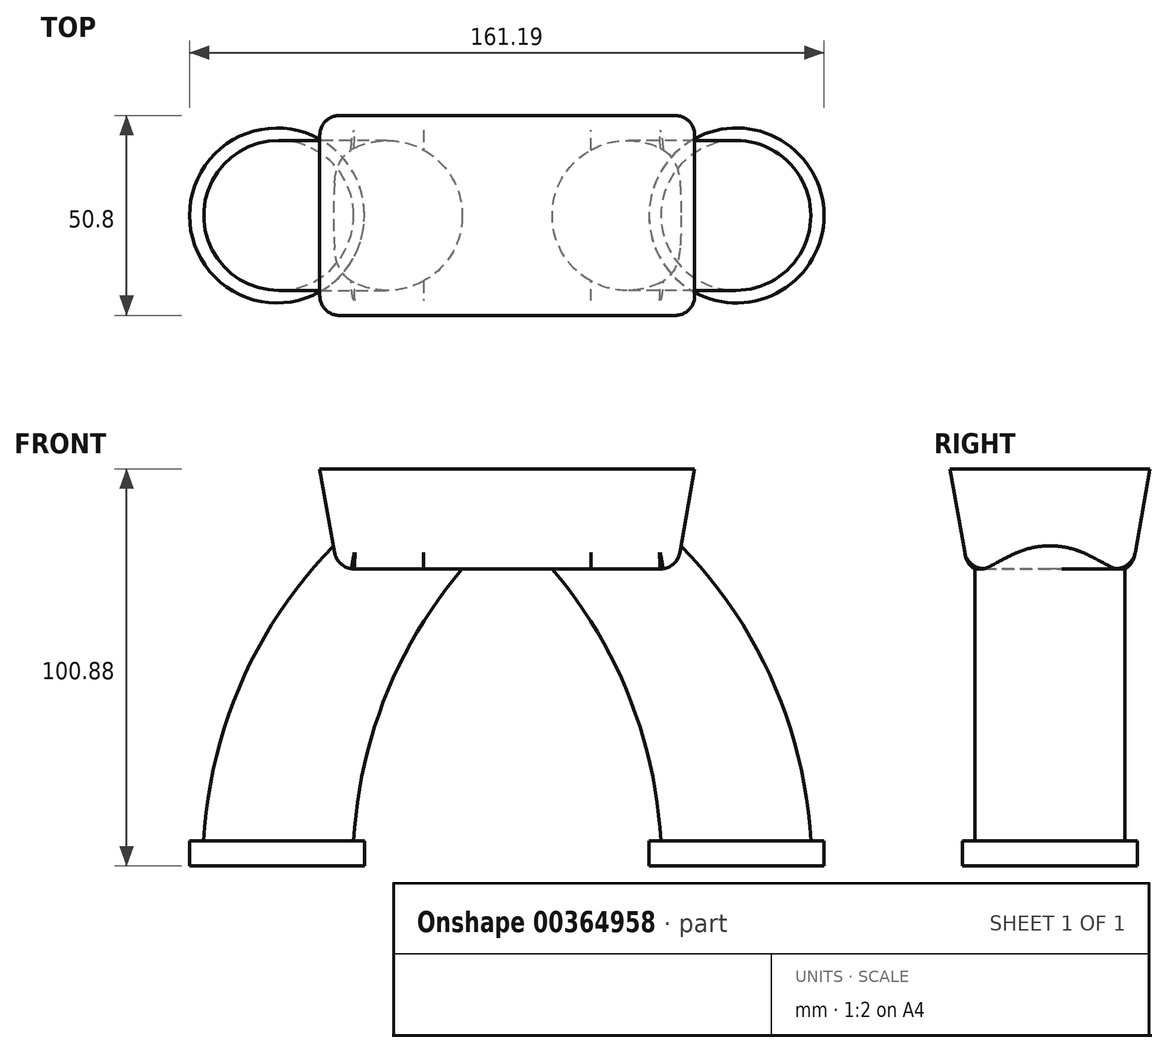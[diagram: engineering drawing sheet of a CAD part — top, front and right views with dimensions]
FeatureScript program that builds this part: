
annotation { "Feature Type Name" : "Feature", "Feature Type Description" : "" }
export const myFeature = defineFeature(function(context is Context, id is Id, definition is map)
    precondition{}
    {
        {
            var Q0;
            Q0=qCreatedBy(makeId("Top.planeOp"),FACE);
            var sketch = newSketch(context, id + "F0", { "sketchPlane" : qUnion([Q0])});
            skLineSegment(sketch, "E0", {"start": v(0, 0) * mm, "end": v(-116.48, 0) * mm, "construction": true});
            skCircle(sketch, "E1", {"center": v(-116.48, 0) * mm, "radius": 19.05 * mm});
            skCircle(sketch, "E2", {"center": v(0, 0) * mm, "radius": 19.05 * mm});
            skLineSegment(sketch, "E3.right", {"start": v(-140, -27.25) * mm, "end": v(-140, 27.25) * mm});
            skPoint(sketch, "E3.middle", {"position": v(-58.24, 0) * mm});
            skPoint(sketch, "E3.left.end.orphan", {"position": v(23.51, 27.25) * mm});
            skPoint(sketch, "E3.left.start.orphan", {"position": v(23.51, -27.25) * mm});
            skSolve(sketch);
        }
        {
            var Q0;
            Q0=qCreatedBy(makeId("Front.planeOp"),FACE);
            var sketch = newSketch(context, id + "F1", { "sketchPlane" : qUnion([Q0])});
            skArc(sketch, "E4", {"start": v(-58.24, 100.88) * mm, "mid": v(-100.88, 58.24) * mm, "end": v(-116.48, 0) * mm});
            skArc(sketch, "E5", {"start": v(0, 0) * mm, "mid": v(-15.6, 58.24) * mm, "end": v(-58.24, 100.88) * mm});
            skSolve(sketch);
        }
        {
            var Q0;
            Q0=makeQuery(id+"F0.imprint","IMPRINT",FACE,{"disambiguationData":[TD([[makeQuery(id+"F0.imprint","IMPRINT",EDGE,{"derivedFrom":sQuery(id+"F0.wireOp",EDGE,"E1")}),1.0]])]});
            var Q1;
            Q1=sQuery(id+"F1.wireOp",EDGE,"E4");
            sweep(context, id + "F2", {"profiles" : qUnion([Q0]), "path" : qUnion([Q1]), "keepProfileOrientation" : true});
        }
        {
            var Q0;
            Q0=makeQuery(id+"F0.imprint","IMPRINT",FACE,{"disambiguationData":[TD([[makeQuery(id+"F0.imprint","IMPRINT",EDGE,{"derivedFrom":sQuery(id+"F0.wireOp",EDGE,"E2")}),1.0]])]});
            var Q1;
            Q1=sQuery(id+"F1.wireOp",EDGE,"E5");
            sweep(context, id + "F3", {"operationType" : NewBodyOperationType.ADD, "profiles" : qUnion([Q0]), "path" : qUnion([Q1]), "keepProfileOrientation" : true});
        }
        {
            var Q0;
            Q0=qCreatedBy(makeId("Top.planeOp"),FACE);
            var sketch = newSketch(context, id + "F4", { "sketchPlane" : qUnion([Q0])});
            skCircle(sketch, "E6", {"center": v(-116.73, 0) * mm, "radius": 22.23 * mm});
            skCircle(sketch, "E7", {"center": v(0, 0) * mm, "radius": 22.23 * mm});
            skSolve(sketch);
        }
        {
            var Q0;
            Q0=makeQuery(id+"F4.imprint","IMPRINT",FACE,{"disambiguationData":[TD([[makeQuery(id+"F4.imprint","IMPRINT",EDGE,{"derivedFrom":sQuery(id+"F4.wireOp",EDGE,"E6")}),1.0]])]});
            var Q1;
            Q1=makeQuery(id+"F4.imprint","IMPRINT",FACE,{"disambiguationData":[TD([[makeQuery(id+"F4.imprint","IMPRINT",EDGE,{"derivedFrom":sQuery(id+"F4.wireOp",EDGE,"E7")}),1.0]])]});
            extrude(context, id + "F5", {"entities" : qUnion([Q0, Q1]), "operationType" : NewBodyOperationType.ADD, "depth" : 6.35 * mm});
        }
        {
            var Q0;
            Q0=makeQuery(id+"F2.opSweep","CAP_FACE",FACE,{"disambiguationData":[OSD([sQuery(id+"F0.wireOp",EDGE,"E1"),sQuery(id+"F1.wireOp",VERTEX,"E4.start")])],"isStart":false});
            var sketch = newSketch(context, id + "F6", { "sketchPlane" : qUnion([Q0])});
            skLineSegment(sketch, "E8.bottom", {"start": v(-32.84, -22.23) * mm, "end": v(-83.64, -22.22) * mm});
            skLineSegment(sketch, "E8.top", {"start": v(-32.84, 22.22) * mm, "end": v(-83.64, 22.23) * mm});
            skLineSegment(sketch, "E8.left", {"start": v(-32.84, -22.23) * mm, "end": v(-32.84, 22.23) * mm});
            skLineSegment(sketch, "E8.right", {"start": v(-83.64, -22.22) * mm, "end": v(-83.64, 22.23) * mm});
            skPoint(sketch, "E8.middle", {"position": v(-58.24, 0) * mm});
            skSolve(sketch);
        }
        {
            var Q0;
            Q0=makeQuery(id+"F6.imprint","IMPRINT",FACE,{"disambiguationData":[TD([[makeQuery(id+"F6.imprint","IMPRINT",EDGE,{"derivedFrom":sQuery(id+"F6.wireOp",EDGE,"E8.bottom")}),-1.0]])]});
            extrude(context, id + "F7", {"entities" : qUnion([Q0]), "operationType" : NewBodyOperationType.ADD, "oppositeDirection" : true, "depth" : 14.48 * mm, "hasSecondDirection" : true, "secondDirectionOppositeDirection" : true, "secondDirectionDepth" : 0.5 * mm, "hasSecondDirectionDraft" : true, "secondDirectionDraftAngle" : 4 * degree, "secondDirectionDraftPullDirection" : true});
        }
        {
            var Q0;
            Q0=makeQuery(id+"F7.opExtrude","CAP_EDGE",EDGE,{"disambiguationData":[OSD([sQuery(id+"F6.wireOp",EDGE,"E8.bottom")])],"isStart":false});
            var Q1;
            Q1=makeQuery(id+"F7.opExtrude","CAP_EDGE",EDGE,{"disambiguationData":[OSD([sQuery(id+"F6.wireOp",EDGE,"E8.top")])],"isStart":false});
            fillet(context, id + "F8", {"entities" : qUnion([Q0, Q1]), "radius" : 5.08 * mm, "tangentPropagation" : true, "allowEdgeOverflow" : false});
        }
        {
            var Q0;
            Q0=makeQuery(id+"F2.opSweep","CAP_FACE",FACE,{"disambiguationData":[OSD([sQuery(id+"F0.wireOp",EDGE,"E1"),sQuery(id+"F1.wireOp",VERTEX,"E4.start")])],"isStart":false});
            var sketch = newSketch(context, id + "F9", { "sketchPlane" : qUnion([Q0])});
            skLineSegment(sketch, "E9.bottom", {"start": v(-10.62, 25.4) * mm, "end": v(-105.87, 25.4) * mm});
            skLineSegment(sketch, "E9.top", {"start": v(-10.62, -25.4) * mm, "end": v(-105.87, -25.4) * mm});
            skLineSegment(sketch, "E9.left", {"start": v(-10.62, 25.4) * mm, "end": v(-10.62, -25.4) * mm});
            skLineSegment(sketch, "E9.right", {"start": v(-105.87, 25.4) * mm, "end": v(-105.87, -25.4) * mm});
            skPoint(sketch, "E9.middle", {"position": v(-58.24, 0) * mm});
            skSolve(sketch);
        }
        {
            var Q0;
            Q0=makeQuery(id+"F9.imprint","IMPRINT",FACE,{"disambiguationData":[TD([[makeQuery(id+"F9.imprint","IMPRINT",EDGE,{"derivedFrom":sQuery(id+"F9.wireOp",EDGE,"E9.bottom")}),1.0]])]});
            var Q1;
            {var subQ0=makeQuery(id+"F2.opSweep","CAP_EDGE",EDGE,{"disambiguationData":[OSD([sQuery(id+"F0.wireOp",EDGE,"E1"),sQuery(id+"F1.wireOp",VERTEX,"E4.start")])],"isStart":false});Q1=makeQuery(id+"F9.imprint","IMPRINT",FACE,{"disambiguationData":[TD([[makeQuery(id+"F9.imprint","IMPRINT",EDGE,{"derivedFrom":makeQuery(id+"F3.boolean.opBoolean","SPLIT",EDGE,{"derivedFrom":subQ0})}),1.0]])]});}
            extrude(context, id + "F10", {"entities" : qUnion([Q0, Q1]), "operationType" : NewBodyOperationType.ADD, "oppositeDirection" : true, "depth" : 25.4 * mm, "hasDraft" : true, "draftAngle" : 10 * degree, "draftPullDirection" : true});
        }
        {
            var Q0;
            Q0=makeQuery(id+"F10.opExtrude","SWEPT_EDGE",EDGE,{"disambiguationData":[OSD([sQuery(id+"F9.wireOp",EDGE,"E9.top"),sQuery(id+"F9.wireOp",EDGE,"E9.left")])]});
            var Q1;
            Q1=makeQuery(id+"F10.opExtrude","SWEPT_EDGE",EDGE,{"disambiguationData":[OSD([sQuery(id+"F9.wireOp",EDGE,"E9.bottom"),sQuery(id+"F9.wireOp",EDGE,"E9.left")])]});
            var Q2;
            {var subQ0=sQuery(id+"F9.wireOp",EDGE,"E9.left");var subQ1=sQuery(id+"F9.wireOp",EDGE,"E9.top");Q2=makeQuery(id+"F10.boolean.opBoolean","SPLIT",EDGE,{"disambiguationData":[TD([makeQuery(id+"F10.opExtrude","SWEPT_FACE",FACE,{"disambiguationData":[OSD([subQ1])]})])],"derivedFrom":makeQuery(id+"F10.opExtrude","CAP_EDGE",EDGE,{"disambiguationData":[OSD([subQ0])],"isStart":false})});}
            var Q3;
            {var subQ0=sQuery(id+"F9.wireOp",EDGE,"E9.left");var subQ1=sQuery(id+"F9.wireOp",EDGE,"E9.bottom");Q3=makeQuery(id+"F10.boolean.opBoolean","SPLIT",EDGE,{"disambiguationData":[TD([makeQuery(id+"F10.opExtrude","SWEPT_FACE",FACE,{"disambiguationData":[OSD([subQ1])]})])],"derivedFrom":makeQuery(id+"F10.opExtrude","CAP_EDGE",EDGE,{"disambiguationData":[OSD([subQ0])],"isStart":false})});}
            var Q4;
            Q4=makeQuery(id+"F10.opExtrude","SWEPT_EDGE",EDGE,{"disambiguationData":[OSD([sQuery(id+"F9.wireOp",EDGE,"E9.top"),sQuery(id+"F9.wireOp",EDGE,"E9.right")])]});
            var Q5;
            {var subQ0=sQuery(id+"F9.wireOp",EDGE,"E9.top");var subQ1=sQuery(id+"F9.wireOp",EDGE,"E9.right");Q5=makeQuery(id+"F10.boolean.opBoolean","SPLIT",EDGE,{"disambiguationData":[TD([makeQuery(id+"F10.opExtrude","SWEPT_FACE",FACE,{"disambiguationData":[OSD([subQ0])]})])],"derivedFrom":makeQuery(id+"F10.opExtrude","CAP_EDGE",EDGE,{"disambiguationData":[OSD([subQ1])],"isStart":false})});}
            var Q6;
            {var subQ0=sQuery(id+"F9.wireOp",EDGE,"E9.bottom");var subQ1=sQuery(id+"F9.wireOp",EDGE,"E9.right");Q6=makeQuery(id+"F10.boolean.opBoolean","SPLIT",EDGE,{"disambiguationData":[TD([makeQuery(id+"F10.opExtrude","SWEPT_FACE",FACE,{"disambiguationData":[OSD([subQ0])]})])],"derivedFrom":makeQuery(id+"F10.opExtrude","CAP_EDGE",EDGE,{"disambiguationData":[OSD([subQ1])],"isStart":false})});}
            var Q7;
            Q7=makeQuery(id+"F10.opExtrude","SWEPT_EDGE",EDGE,{"disambiguationData":[OSD([sQuery(id+"F9.wireOp",EDGE,"E9.bottom"),sQuery(id+"F9.wireOp",EDGE,"E9.right")])]});
            fillet(context, id + "F11", {"entities" : qUnion([Q0, Q1, Q2, Q3, Q4, Q5, Q6, Q7]), "radius" : 5.08 * mm, "tangentPropagation" : true, "allowEdgeOverflow" : false});
        }
        {
            var Q0;
            Q0=makeQuery(id+"F10.opExtrude","CAP_EDGE",EDGE,{"disambiguationData":[OSD([sQuery(id+"F9.wireOp",EDGE,"E9.bottom")])],"isStart":false});
            var Q1;
            Q1=makeQuery(id+"F10.opExtrude","CAP_EDGE",EDGE,{"disambiguationData":[OSD([sQuery(id+"F9.wireOp",EDGE,"E9.top")])],"isStart":false});
            fillet(context, id + "F12", {"entities" : qUnion([Q0, Q1]), "radius" : 5.08 * mm, "tangentPropagation" : true, "allowEdgeOverflow" : false});
        }
    });
